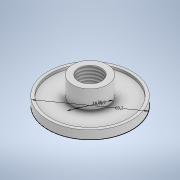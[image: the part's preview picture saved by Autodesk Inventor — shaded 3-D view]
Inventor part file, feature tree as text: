
AUTODESK INVENTOR PART (.ipt)
format: ipt  version: 2022 (Build 260153000, 153)  size: 128,000 bytes
history: native  units: mm
features: extrude x3, sketch x2, other x1, thread x1
ambient origin geometry x8: Origin, YZ Plane, XZ Plane, XY Plane, X Axis, Y Axis, Z Axis, Center Point
bodies: Body1 (feature_tree)
feature tree (7):
  other  "Sólido1"
  sketch  "Boceto1"  dims[d0=69.2mm d1=18.97mm]
  extrude  "Extrusión1"  Depth=18.97mm
  extrude  "Extrusión2"  Depth=21.97mm TaperAngle=0.0deg
  thread  "Rosca1"  [1 undecoded]
  extrude  "Extrusión3"  Depth=21.97mm TaperAngle=0.0deg
  sketch  "Boceto2"  dims[d2=28.9mm d3=21.97mm d4=0.0mm d5=6.95mm d6=0.0mm d7=21.97mm d8=0.0mm d9=64.3mm d10=2.0mm d11=0.0mm]
note: 1 required parameter value undecoded (feature->parameter linkage not recoverable at this tier; creation-order binding heuristic only, values carry confidence <= 0.55)
